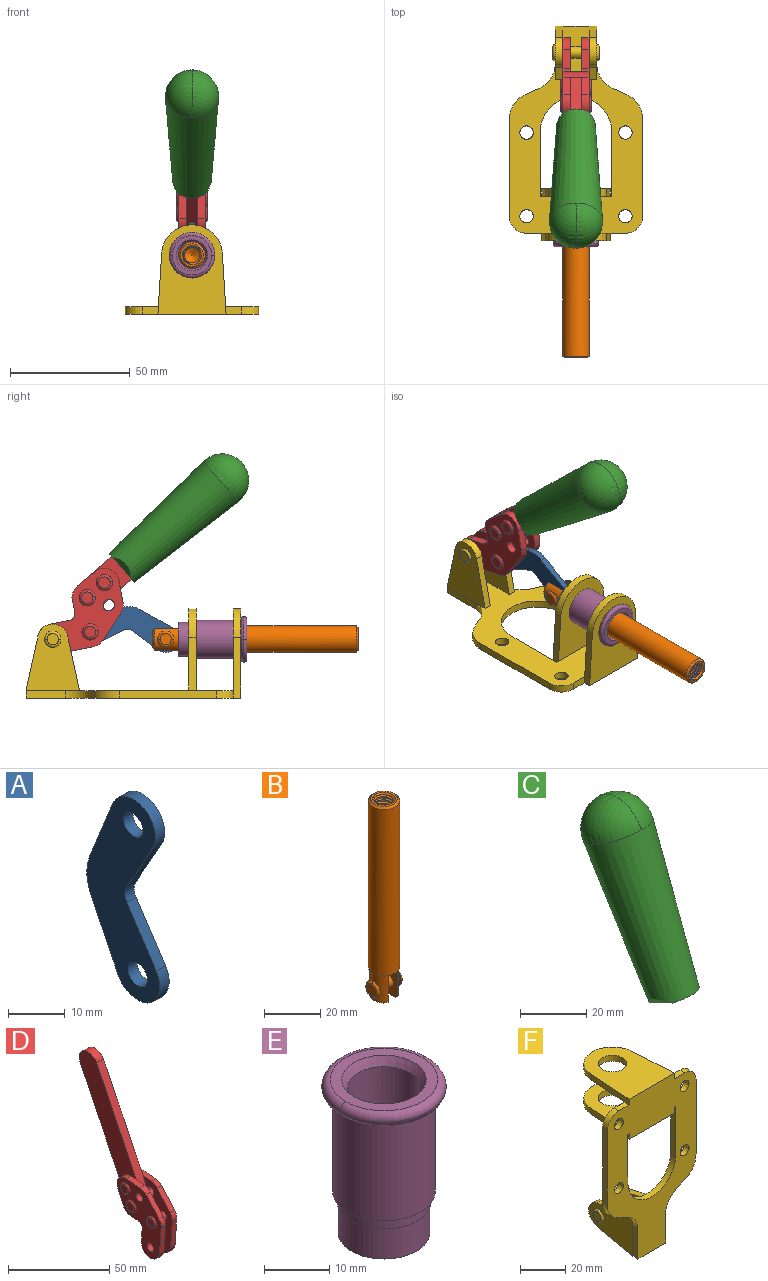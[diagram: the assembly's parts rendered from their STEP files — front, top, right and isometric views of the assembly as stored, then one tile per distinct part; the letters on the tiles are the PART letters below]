
ASSEMBLY  parts=6 mates=6
PART A: 12 faces, bbox 2.3x18.2x42.8 mm
  f0: cylinder r=2.4mm len=4.8mm, axis (1,0,0), area 34.9mm2, adj f4,f11
  f1: cylinder r=10.41mm len=8.47mm, axis (1,0,0), area 20.2mm2, adj f4,f9,f10,f11
  f2: cylinder r=3.05mm len=3.16mm, axis (1,0,0), area 7.7mm2, adj f4,f6,f7,f11
  f3: cylinder r=2.4mm len=4.8mm, axis (1,0,0), area 34.9mm2, adj f4,f11
  f4: plane 42.81x18.23mm, normal (-1,0,0), area 414.1mm2, adj f0,f1,f2,f3,f5,f6,f7,f8
  f5: cylinder r=5.54mm len=10.67mm, axis (1,0,0), area 41.8mm2, adj f4,f6,f10,f11
  f6: plane 11.66x6.53mm, normal (0,-0.87,-0.49), area 30.9mm2, adj f2,f4,f5,f11
  f7: plane 11.17x7.33mm, normal (0,-0.84,0.55), area 30.9mm2, adj f2,f4,f8,f11
  f8: cylinder r=5.54mm len=10.51mm, axis (1,0,0), area 41.8mm2, adj f4,f7,f9,f11
  f9: plane 13.67x6.67mm, normal (0,0.9,-0.44), area 35.1mm2, adj f1,f4,f8,f11
  f10: plane 14.1x5.7mm, normal (0,0.93,0.37), area 35.1mm2, adj f1,f4,f5,f11
  f11: plane 42.81x18.23mm, normal (1,0,0), area 414.1mm2, adj f0,f1,f2,f3,f5,f6,f7,f8
PART B: 48 faces, bbox 12.6x11.1x86.1 mm
  f0: torus R=2.41mm, axis (-1,0,0), area 15mm2, adj f30,f32,f34
  f1: torus R=2.41mm, axis (-1,0,0), area 15mm2, adj f29,f31,f33
  f2: cylinder r=5.54mm len=72.39mm, axis (0,0,1), area 2518.5mm2, adj f3,f4,f42,f43
  f3: cone r=5.54mm half-angle=45deg, axis (0,0,1), area 7.6mm2, adj f2,f5,f41
  f4: cone r=5.54mm half-angle=45deg, axis (0,0,-1), area 34.9mm2, adj f2,f39
  f5: cylinder r=5.08mm len=11.48mm, axis (0,0,1), area 108.3mm2, adj f3,f7,f8,f41
  f6: cylinder r=2.41mm len=4.83mm, axis (-1,0,0), area 71.2mm2, adj f40,f41
  f7: cylinder r=2.41mm len=4.83mm, axis (-1,0,0), area 7.6mm2, adj f5,f34
  f8: cone r=5.08mm half-angle=45deg, axis (0,0,1), area 10.6mm2, adj f5,f37,f41
  f9: cone r=3.98mm half-angle=45deg, axis (0,0,1), area 17.6mm2, adj f27,f39,f45,f46,f47
  f10: cylinder r=2.41mm len=4.83mm, axis (-1,0,0), area 7.6mm2, adj f33,f38
  f11: cylinder r=3.2mm len=6.4mm, axis (0,0,1), area 78.4mm2, adj f12,f28,f44,f45,f47
  f12: cylinder r=3.2mm len=6.4mm, axis (0,0,1), area 10.5mm2, adj f11,f13,f45,f47
  f13: cylinder r=3.2mm len=6.4mm, axis (0,0,1), area 10.5mm2, adj f12,f14,f45,f47
  f14: cylinder r=3.2mm len=6.4mm, axis (0,0,1), area 10.5mm2, adj f13,f15,f45,f47
  f15: cylinder r=3.2mm len=6.4mm, axis (0,0,1), area 10.5mm2, adj f14,f16,f45,f47
  f16: cylinder r=3.2mm len=6.4mm, axis (0,0,1), area 10.5mm2, adj f15,f17,f45,f47
  f17: cylinder r=3.2mm len=6.4mm, axis (0,0,1), area 10.5mm2, adj f16,f18,f45,f47
  f18: cylinder r=3.2mm len=6.4mm, axis (0,0,1), area 10.5mm2, adj f17,f19,f45,f47
  f19: cylinder r=3.2mm len=6.4mm, axis (0,0,1), area 10.5mm2, adj f18,f20,f45,f47
  f20: cylinder r=3.2mm len=6.4mm, axis (0,0,1), area 10.5mm2, adj f19,f21,f45,f47
  f21: cylinder r=3.2mm len=6.4mm, axis (0,0,1), area 10.5mm2, adj f20,f22,f45,f47
  f22: cylinder r=3.2mm len=6.4mm, axis (0,0,1), area 10.5mm2, adj f21,f23,f45,f47
  f23: cylinder r=3.2mm len=6.4mm, axis (0,0,1), area 10.5mm2, adj f22,f24,f45,f47
  f24: cylinder r=3.2mm len=6.4mm, axis (0,0,1), area 10.5mm2, adj f23,f25,f45,f47
  f25: cylinder r=3.2mm len=6.4mm, axis (0,0,1), area 10.5mm2, adj f24,f26,f45,f47
  f26: cylinder r=3.2mm len=6.4mm, axis (0,0,1), area 10.5mm2, adj f25,f27,f45,f47
  f27: cylinder r=3.2mm len=6.4mm, axis (0,0,1), area 7.4mm2, adj f9,f26,f45,f47
  f28: cone r=3.2mm half-angle=60deg, axis (0,0,1), area 37.2mm2, adj f11
  f29: plane 4.83x4.83mm, normal (-1,0,0), area 18.3mm2, adj f1,f31
  f30: plane 4.83x4.83mm, normal (1,0,0), area 18.3mm2, adj f0,f32
  f31: torus R=2.41mm, axis (-1,0,0), area 15mm2, adj f1,f29,f33
  f32: torus R=2.41mm, axis (-1,0,0), area 15mm2, adj f0,f30,f34
  f33: plane 6.83x6.83mm, normal (1,0,0), area 18.3mm2, adj f1,f10,f31
  f34: plane 6.83x6.83mm, normal (-1,0,0), area 18.3mm2, adj f0,f7,f32
  f35: cone r=5.08mm half-angle=45deg, axis (0,0,1), area 10.6mm2, adj f36,f38,f40
  f36: plane 7.25x1.97mm, normal (0,0,-1), area 10mm2, adj f35,f40
  f37: plane 7.25x1.97mm, normal (0,0,-1), area 10mm2, adj f8,f41
  f38: cylinder r=5.08mm len=11.48mm, axis (0,0,1), area 108.3mm2, adj f10,f35,f40,f42
  f39: plane 9.55x9.55mm, normal (0,0,1), area 22mm2, adj f4,f9
  f40: plane 12.76x10.09mm, normal (1,0,0), area 95.7mm2, adj f6,f35,f36,f38,f42,f43
  f41: plane 12.76x10.09mm, normal (-1,0,0), area 95.7mm2, adj f3,f5,f6,f8,f37,f43
  f42: cone r=5.54mm half-angle=45deg, axis (0,0,1), area 7.6mm2, adj f2,f38,f40
  f43: plane 11.07x4.7mm, normal (0,0,-1), area 50.4mm2, adj f2,f40,f41
  f44: plane 0.89x0.62mm, normal (-1,0,0), area 0.3mm2, adj f11,f45,f46,f47
  f45: bspline ~24.8x7.63mm, area 266.6mm2, adj f9,f11,f12,f13,f14,f15,f16,f17
  f46: bspline ~24.87x7.63mm, area 73.6mm2, adj f9,f44,f45,f47
  f47: bspline ~24.98x7.63mm, area 272.5mm2, adj f9,f11,f12,f13,f14,f15,f16,f17
PART C: 11 faces, bbox 22.3x42.6x64.5 mm
  f0: sphere r=11.13mm, area 411.4mm2, adj f1,f8
  f1: cone r=11.11mm half-angle=3.3deg, axis (0,0.44,0.9), area 3251.8mm2, adj f0,f7,f8,f9,f10
  f2: cylinder r=6.16mm len=11.7mm, axis (1,0,0), area 89.5mm2, adj f3,f4,f5,f6
  f3: plane 60.23x36.75mm, normal (-1,0,0), area 763.6mm2, adj f2,f4,f6,f10
  f4: plane 51.37x25.05mm, normal (0,0.9,-0.44), area 264.2mm2, adj f2,f3,f5,f10
  f5: plane 60.23x36.75mm, normal (1,0,0), area 763.6mm2, adj f2,f4,f6,f10
  f6: plane 51.37x25.05mm, normal (0,-0.9,0.44), area 264.2mm2, adj f2,f3,f5,f10
  f7: plane 9.95x5.95mm, normal (0.71,-0.31,-0.64), area 25.8mm2, adj f1,f10
  f8: sphere r=11.13mm, area 411.4mm2, adj f0,f1
  f9: plane 9.95x5.95mm, normal (-0.71,-0.31,-0.64), area 25.8mm2, adj f1,f10
  f10: plane 14.27x11.38mm, normal (0,-0.44,-0.9), area 106.7mm2, adj f1,f3,f4,f5,f6,f7,f9
PART D: 59 faces, bbox 12.9x60.2x99.6 mm
  f0: torus R=2.39mm, axis (-1,0,0), area 14.9mm2, adj f20,f43,f51
  f1: torus R=2.39mm, axis (-1,0,0), area 14.9mm2, adj f19,f42,f51
  f2: torus R=2.39mm, axis (-1,0,0), area 14.9mm2, adj f18,f35,f51
  f3: torus R=2.39mm, axis (-1,0,0), area 14.9mm2, adj f14,f17,f23
  f4: torus R=2.39mm, axis (-1,0,0), area 14.9mm2, adj f13,f16,f23
  f5: torus R=2.39mm, axis (-1,0,0), area 14.9mm2, adj f12,f15,f23
  f6: cylinder r=2.39mm len=4.78mm, axis (1,0,0), area 46.5mm2, adj f48,f50,f51
  f7: cylinder r=2.39mm len=4.78mm, axis (1,0,0), area 46.5mm2, adj f50,f51
  f8: cylinder r=6.35mm len=12.68mm, axis (1,0,0), area 61.8mm2, adj f38,f39,f50,f51
  f9: cylinder r=2.39mm len=4.78mm, axis (-1,0,0), area 70.5mm2, adj f46,f50
  f10: cylinder r=2.39mm len=4.78mm, axis (-1,0,0), area 46.5mm2, adj f23,f45,f46
  f11: cylinder r=2.39mm len=4.78mm, axis (-1,0,0), area 46.5mm2, adj f23,f46
  f12: plane 4.78x4.78mm, normal (1,0,0), area 17.9mm2, adj f5,f15
  f13: plane 4.78x4.78mm, normal (1,0,0), area 17.9mm2, adj f4,f16
  f14: plane 4.78x4.78mm, normal (1,0,0), area 17.9mm2, adj f3,f17
  f15: torus R=2.39mm, axis (-1,0,0), area 14.9mm2, adj f5,f12,f23
  f16: torus R=2.39mm, axis (-1,0,0), area 14.9mm2, adj f4,f13,f23
  f17: torus R=2.39mm, axis (-1,0,0), area 14.9mm2, adj f3,f14,f23
  f18: plane 4.78x4.78mm, normal (-1,0,0), area 17.9mm2, adj f2,f35
  f19: plane 4.78x4.78mm, normal (-1,0,0), area 17.9mm2, adj f1,f42
  f20: plane 4.78x4.78mm, normal (-1,0,0), area 17.9mm2, adj f0,f43
  f21: plane 2.26x0.2mm, normal (1,0,0), area 0.2mm2, adj f31,f44
  f22: plane 2.26x0.2mm, normal (-1,0,0), area 0.2mm2, adj f41,f44
  f23: plane 39.37x30.77mm, normal (1,0,0), area 565.5mm2, adj f3,f4,f5,f10,f11,f15,f16,f17
  f24: cylinder r=6.1mm len=4.15mm, axis (-1,0,0), area 14.7mm2, adj f23,f25,f32,f46
  f25: plane 10.25x9.01mm, normal (0,-0.75,0.66), area 42.3mm2, adj f23,f24,f26,f46
  f26: cylinder r=6.35mm len=4.64mm, axis (-1,0,0), area 15.6mm2, adj f23,f25,f27,f46
  f27: plane 15.84x3.1mm, normal (0,-1,-0.07), area 49.2mm2, adj f23,f26,f28,f46
  f28: cylinder r=6.35mm len=12.68mm, axis (-1,0,0), area 61.8mm2, adj f23,f27,f29,f46
  f29: plane 8.11x3.1mm, normal (0,1,0.07), area 25.2mm2, adj f23,f28,f30,f46
  f30: cylinder r=3.05mm len=3.25mm, axis (-1,0,0), area 14.8mm2, adj f23,f29,f31,f46
  f31: plane 5.99x3.1mm, normal (0,0.07,-1), area 18.6mm2, adj f21,f23,f30,f44,f46
  f32: plane 9.5x3.1mm, normal (0,-0.07,1), area 29.5mm2, adj f23,f24,f33,f46,f47
  f33: cylinder r=6.1mm len=8.63mm, axis (-1,0,0), area 39.1mm2, adj f23,f32,f34,f47
  f34: plane 8.65x3.96mm, normal (0,0.91,-0.42), area 29.5mm2, adj f23,f33,f44,f47
  f35: torus R=2.39mm, axis (-1,0,0), area 14.9mm2, adj f2,f18,f51
  f36: plane 10.25x9.01mm, normal (0,-0.75,0.66), area 42.3mm2, adj f37,f49,f50,f51
  f37: cylinder r=6.35mm len=4.64mm, axis (1,0,0), area 15.6mm2, adj f36,f38,f50,f51
  f38: plane 15.84x3.1mm, normal (0,-1,-0.07), area 49.2mm2, adj f8,f37,f50,f51
  f39: plane 8.11x3.1mm, normal (0,1,0.07), area 25.2mm2, adj f8,f40,f50,f51
  f40: cylinder r=3.05mm len=3.25mm, axis (1,0,0), area 14.8mm2, adj f39,f41,f50,f51
  f41: plane 5.99x3.1mm, normal (0,0.07,-1), area 18.6mm2, adj f22,f40,f44,f50,f51
  f42: torus R=2.39mm, axis (-1,0,0), area 14.9mm2, adj f1,f19,f51
  f43: torus R=2.39mm, axis (-1,0,0), area 14.9mm2, adj f0,f20,f51
  f44: cylinder r=6.35mm len=12.12mm, axis (-1,0,0), area 128.9mm2, adj f21,f22,f23,f31,f34,f41,f46,f47
  f45: plane 2.65x1.35mm, normal (1,0,0), area 1mm2, adj f10,f55
  f46: plane 39.08x20.42mm, normal (-1,0,0), area 412.5mm2, adj f9,f10,f11,f24,f25,f26,f27,f28
  f47: plane 77.62x39.82mm, normal (1,0,0), area 850mm2, adj f32,f33,f34,f44,f53,f54,f55
  f48: plane 2.65x1.35mm, normal (-1,0,0), area 1mm2, adj f6,f55
  f49: cylinder r=6.1mm len=4.15mm, axis (1,0,0), area 14.7mm2, adj f36,f50,f51,f56
  f50: plane 39.08x20.42mm, normal (1,0,0), area 412.5mm2, adj f6,f7,f8,f9,f36,f37,f38,f39
  f51: plane 39.37x30.77mm, normal (-1,0,0), area 565.5mm2, adj f0,f1,f2,f6,f7,f8,f35,f36
  f52: plane 8.65x3.96mm, normal (0,0.91,-0.42), area 29.5mm2, adj f44,f51,f57,f58
  f53: plane 68.49x33.4mm, normal (0,0.9,-0.44), area 358.1mm2, adj f44,f47,f54,f58
  f54: cylinder r=6.35mm len=12.06mm, axis (1,0,0), area 93.7mm2, adj f47,f53,f55,f58
  f55: plane 68.49x33.4mm, normal (0,-0.9,0.44), area 358.1mm2, adj f44,f45,f46,f47,f48,f50,f54,f58
  f56: plane 9.5x3.1mm, normal (0,-0.07,1), area 29.5mm2, adj f49,f50,f51,f57,f58
  f57: cylinder r=6.1mm len=8.63mm, axis (1,0,0), area 39.1mm2, adj f51,f52,f56,f58
  f58: plane 77.62x39.82mm, normal (-1,0,0), area 850mm2, adj f44,f52,f53,f54,f55,f56,f57
PART E: 15 faces, bbox 20.6x20.6x28.7 mm
  f0: torus R=8.26mm, axis (0,0,1), area 56.8mm2, adj f1,f10,f12
  f1: torus R=8.26mm, axis (0,0,1), area 56.8mm2, adj f0,f6,f13
  f2: cylinder r=5.59mm len=25.91mm, axis (0,0,1), area 909.6mm2, adj f3,f4
  f3: cone r=6.86mm half-angle=45deg, axis (0,0,-1), area 70.2mm2, adj f2,f14
  f4: cone r=6.47mm half-angle=30deg, axis (0,0,1), area 66.7mm2, adj f2,f13
  f5: cylinder r=7.04mm len=14.07mm, axis (0,0,1), area 252.6mm2, adj f11,f14
  f6: torus R=8.26mm, axis (0,0,1), area 56.8mm2, adj f1,f12,f13
  f7: cylinder r=7.16mm len=14.33mm, axis (0,0,1), area 91.5mm2, adj f9,f11
  f8: cylinder r=7.86mm len=18.42mm, axis (0,0,1), area 909.6mm2, adj f9,f10
  f9: plane 15.72x15.72mm, normal (0,0,-1), area 33mm2, adj f7,f8
  f10: plane 16.51x16.51mm, normal (0,0,-1), area 19.9mm2, adj f0,f8,f12
  f11: plane 14.33x14.33mm, normal (0,0,-1), area 5.7mm2, adj f5,f7
  f12: torus R=8.26mm, axis (0,0,1), area 56.8mm2, adj f0,f6,f10
  f13: plane 16.51x16.51mm, normal (0,0,1), area 82.7mm2, adj f1,f4,f6
  f14: plane 14.07x14.07mm, normal (0,0,-1), area 7.8mm2, adj f3,f5
PART F: 55 faces, bbox 55.7x37.4x89.8 mm
  f0: torus R=2.41mm, axis (-1,0,0), area 15mm2, adj f11,f15,f25
  f1: torus R=2.41mm, axis (-1,0,0), area 15mm2, adj f10,f12,f22
  f2: cylinder r=2.78mm len=5.56mm, axis (0,-1,0), area 54.2mm2, adj f30,f54
  f3: cylinder r=14.99mm len=29.97mm, axis (0,-1,0), area 145.9mm2, adj f30,f49,f53,f54
  f4: cylinder r=2.78mm len=5.56mm, axis (0,-1,0), area 54.2mm2, adj f30,f54
  f5: cylinder r=2.78mm len=5.56mm, axis (0,-1,0), area 54.2mm2, adj f30,f54
  f6: cylinder r=2.78mm len=5.56mm, axis (0,-1,0), area 54.2mm2, adj f30,f54
  f7: cylinder r=6.35mm len=12.7mm, axis (0,0,1), area 123.6mm2, adj f27,f51
  f8: cylinder r=6.35mm len=12.7mm, axis (0,0,-1), area 124.7mm2, adj f21,f35
  f9: cylinder r=2.41mm len=11.18mm, axis (-1,0,0), area 169.4mm2, adj f16,f19
  f10: plane 4.83x4.83mm, normal (1,0,0), area 18.3mm2, adj f1,f12
  f11: plane 4.83x4.83mm, normal (-1,0,0), area 18.3mm2, adj f0,f15
  f12: torus R=2.41mm, axis (-1,0,0), area 15mm2, adj f1,f10,f22
  f13: cylinder r=6.35mm len=12.41mm, axis (1,0,0), area 53.4mm2, adj f18,f19,f22,f23
  f14: cylinder r=6.35mm len=12.41mm, axis (-1,0,0), area 53.4mm2, adj f16,f17,f24,f25
  f15: torus R=2.41mm, axis (-1,0,0), area 15mm2, adj f0,f11,f25
  f16: plane 27.86x22.35mm, normal (1,0,0), area 425.4mm2, adj f9,f14,f17,f24,f30
  f17: plane 22.86x4.97mm, normal (0,0.21,0.98), area 72.5mm2, adj f14,f16,f25,f30
  f18: plane 22.86x4.97mm, normal (0,0.21,0.98), area 72.5mm2, adj f13,f19,f22,f30
  f19: plane 27.86x22.35mm, normal (-1,0,0), area 425.4mm2, adj f9,f13,f18,f23,f30
  f20: cylinder r=12.7mm len=25.35mm, axis (0,0,-1), area 119.8mm2, adj f21,f34,f35,f36
  f21: plane 34.21x28.07mm, normal (0,0,-1), area 702.4mm2, adj f8,f20,f30,f34,f36
  f22: plane 27.96x22.45mm, normal (1,0,0), area 407.2mm2, adj f1,f12,f13,f18,f23,f30,f42,f43
  f23: plane 22.86x4.97mm, normal (0,0.21,-0.98), area 72.5mm2, adj f13,f19,f22,f44
  f24: plane 22.86x4.97mm, normal (0,0.21,-0.98), area 72.5mm2, adj f14,f16,f25,f44
  f25: plane 27.86x22.35mm, normal (-1,0,0), area 407.1mm2, adj f0,f14,f15,f17,f24,f30,f45,f46
  f26: plane 3.1x0.95mm, normal (0,0,-1), area 2.7mm2, adj f30,f49,f50,f54
  f27: plane 34.21x28.07mm, normal (0,0,1), area 702.4mm2, adj f7,f28,f30,f50,f52
  f28: cylinder r=12.7mm len=25.35mm, axis (0,0,1), area 118.8mm2, adj f27,f50,f51,f52
  f29: plane 3.1x0.95mm, normal (0,0,-1), area 2.7mm2, adj f30,f52,f53,f54
  f30: plane 86.54x55.63mm, normal (0,1,0), area 2362.9mm2, adj f2,f3,f4,f5,f6,f16,f17,f18
  f31: plane 40.56x3.1mm, normal (-1,0,0), area 125.7mm2, adj f30,f32,f48,f54
  f32: cylinder r=7.11mm len=7.11mm, axis (0,-1,0), area 34.6mm2, adj f30,f31,f33,f54
  f33: plane 6.67x3.1mm, normal (0,0,1), area 20.4mm2, adj f30,f32,f34,f54
  f34: plane 25.39x3.13mm, normal (-1,0.06,0), area 79.5mm2, adj f20,f21,f33,f35,f54
  f35: plane 37.31x28.45mm, normal (0,0,1), area 789.9mm2, adj f8,f20,f34,f36,f54
  f36: plane 25.39x3.13mm, normal (1,0.06,0), area 79.5mm2, adj f20,f21,f35,f37,f54
  f37: plane 6.67x3.1mm, normal (0,0,1), area 20.4mm2, adj f30,f36,f38,f54
  f38: cylinder r=7.11mm len=7.11mm, axis (0,-1,0), area 34.6mm2, adj f30,f37,f39,f54
  f39: plane 40.56x3.1mm, normal (1,0,0), area 125.7mm2, adj f30,f38,f40,f54
  f40: cylinder r=11.18mm len=10.16mm, axis (0,-1,0), area 39.5mm2, adj f30,f39,f41,f54
  f41: plane 6.09x3.1mm, normal (0.42,0,-0.91), area 20.8mm2, adj f30,f40,f42,f54
  f42: cylinder r=11.18mm len=9.41mm, axis (0,-1,0), area 37.2mm2, adj f22,f30,f41,f43,f54
  f43: plane 16.5x3.1mm, normal (1,0,0), area 51.1mm2, adj f22,f42,f44,f54
  f44: plane 17.37x3.1mm, normal (0,0,-1), area 53.8mm2, adj f23,f24,f30,f43,f45,f54
  f45: plane 16.5x3.1mm, normal (-1,0,0), area 51.1mm2, adj f25,f44,f46,f54
  f46: cylinder r=11.18mm len=9.41mm, axis (0,-1,0), area 37.2mm2, adj f25,f30,f45,f47,f54
  f47: plane 6.09x3.1mm, normal (-0.42,0,-0.91), area 20.8mm2, adj f30,f46,f48,f54
  f48: cylinder r=11.18mm len=10.16mm, axis (0,-1,0), area 39.5mm2, adj f30,f31,f47,f54
  f49: plane 26.54x3.1mm, normal (-1,0,0), area 82.3mm2, adj f3,f26,f30,f54
  f50: plane 25.39x3.1mm, normal (1,0.06,0), area 78.8mm2, adj f26,f27,f28,f51,f54
  f51: plane 37.31x28.45mm, normal (0,0,-1), area 789.9mm2, adj f7,f28,f50,f52,f54
  f52: plane 25.39x3.1mm, normal (-1,0.06,0), area 78.8mm2, adj f27,f28,f29,f51,f54
  f53: plane 26.54x3.1mm, normal (1,0,0), area 82.3mm2, adj f3,f29,f30,f54
  f54: plane 89.66x55.63mm, normal (0,-1,0), area 2678.5mm2, adj f2,f3,f4,f5,f6,f26,f29,f31
PLACE A rot(axis=(1,0,0),97.5deg) t=(0,12.59,2.22)mm
PLACE B rot(axis=(1,0,0),90deg) t=(0,9.52,0)mm
PLACE C rot(axis=(1,0,0),75deg) t=(0,3.86,9.14)mm
PLACE D rot(axis=(1,0,0),75deg) t=(0,3.86,9.14)mm
PLACE E rot(axis=(1,0,0),90deg) t=(0,9.14,0)mm
PLACE F rot(axis=(1,0,0),90deg) t=(0,9.14,0)mm fixed
MATE revolute B.f6 <-> A.f5  axis (-1,0,0) through (0,-5.96,24.61)mm
MATE slider B.f2 <-> F.f7  axis (0,-1,0) through (0,-49.26,24.61)mm
MATE fastened E.f0 <-> F.f7  axis (0,1,0) through (0,-37.25,24.61)mm
MATE revolute A.f3 <-> D.f4  axis (1,0,0) through (0,25.65,27.64)mm
MATE fastened D.f54 <-> C.f2  axis (1,0,0) through (0,-30.66,91.94)mm
MATE revolute F.f0 <-> D.f7  axis (-1,0,0) through (0,41.23,24.61)mm
